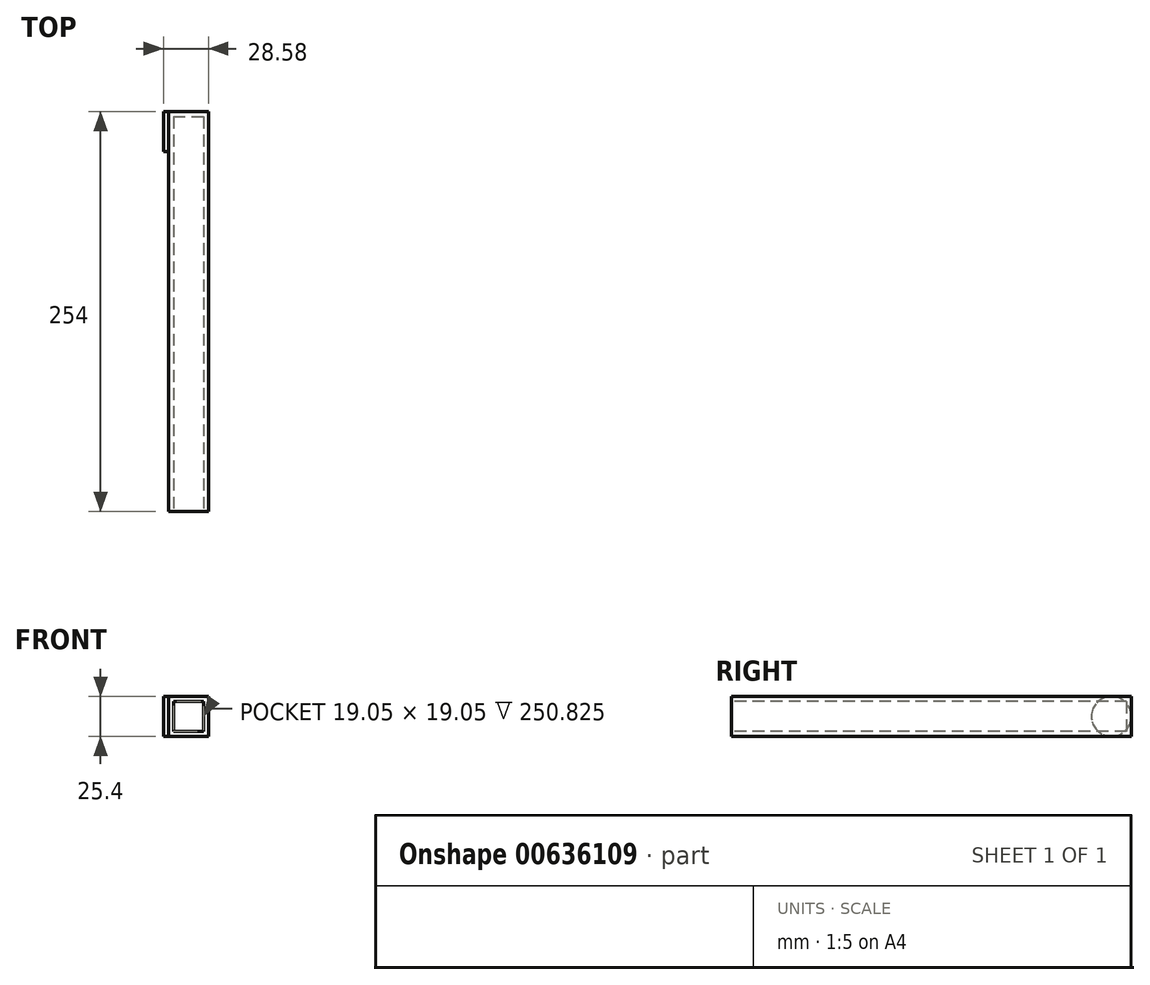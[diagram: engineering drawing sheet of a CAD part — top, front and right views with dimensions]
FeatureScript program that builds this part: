
annotation { "Feature Type Name" : "Feature", "Feature Type Description" : "" }
export const myFeature = defineFeature(function(context is Context, id is Id, definition is map)
    precondition{}
    {
        {
            var Q0;
            Q0=qCreatedBy(makeId("Top.planeOp"),FACE);
            var sketch = newSketch(context, id + "F0", { "sketchPlane" : qUnion([Q0])});
            skLineSegment(sketch, "E0.bottom", {"start": v(-10.66, 215.85) * mm, "end": v(14.74, 215.85) * mm});
            skLineSegment(sketch, "E0.top", {"start": v(-10.66, -38.15) * mm, "end": v(14.74, -38.15) * mm});
            skLineSegment(sketch, "E0.left", {"start": v(-10.66, 215.85) * mm, "end": v(-10.66, -38.15) * mm});
            skLineSegment(sketch, "E0.right", {"start": v(14.74, 215.85) * mm, "end": v(14.74, -38.15) * mm});
            skSolve(sketch);
        }
        {
            var Q0;
            Q0=makeQuery(id+"F0.imprint","IMPRINT",FACE,{"disambiguationData":[TD([[makeQuery(id+"F0.imprint","IMPRINT",EDGE,{"derivedFrom":sQuery(id+"F0.wireOp",EDGE,"E0.bottom")}),-1.0]])]});
            extrude(context, id + "F1", {"entities" : qUnion([Q0]), "depth" : 25.4 * mm, "offsetDistance" : 25.4 * mm});
        }
        {
            var Q0;
            Q0=makeQuery(id+"F1.opExtrude","SWEPT_FACE",FACE,{"disambiguationData":[OSD([sQuery(id+"F0.wireOp",EDGE,"E0.top")])]});
            shell(context, id + "F2", {"entities" : qUnion([Q0]), "thickness" : 3.17 * mm});
        }
        {
            var Q0;
            Q0=makeQuery(id+"F1.opExtrude","SWEPT_FACE",FACE,{"disambiguationData":[OSD([sQuery(id+"F0.wireOp",EDGE,"E0.left")])]});
            var sketch = newSketch(context, id + "F3", { "sketchPlane" : qUnion([Q0])});
            skCircle(sketch, "E1", {"center": v(-203.15, 12.7) * mm, "radius": 12.7 * mm});
            skPoint(sketch, "E2.end.orphan", {"position": v(-203.15, 25.4) * mm});
            skSolve(sketch);
        }
        {
            var Q0;
            {var subQ0=sQuery(id+"F3.wireOp",EDGE,"E1");var subQ1=sQuery(id+"F0.wireOp",EDGE,"E0.left");var subQ3=makeQuery(id+"F3.imprint","INTERSECT",VERTEX,{"derivedFrom":[makeQuery(id+"F1.opExtrude","CAP_EDGE",EDGE,{"disambiguationData":[OSD([subQ1])],"isStart":false}),subQ0]});Q0=makeQuery(id+"F3.imprint","IMPRINT",FACE,{"disambiguationData":[TD([[makeQuery(id+"F3.imprint","IMPRINT",EDGE,{"disambiguationData":[TD([[subQ3,1.0]])],"derivedFrom":subQ0}),1.0]])]});}
            extrude(context, id + "F4", {"entities" : qUnion([Q0]), "operationType" : NewBodyOperationType.ADD, "depth" : 3.17 * mm, "offsetDistance" : 25.4 * mm});
        }
    });
